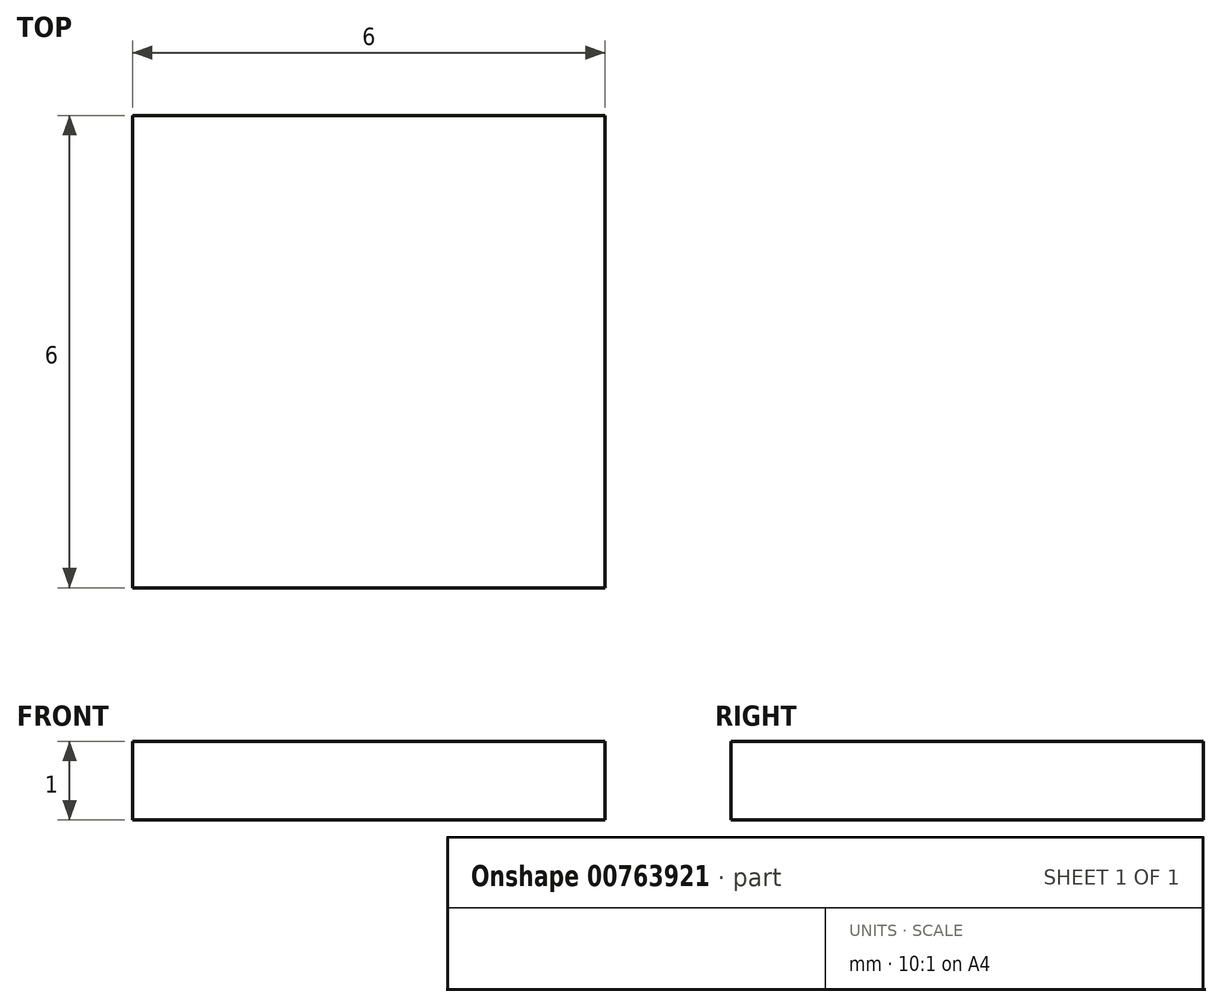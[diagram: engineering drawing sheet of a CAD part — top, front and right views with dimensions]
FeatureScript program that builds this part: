
annotation { "Feature Type Name" : "Feature", "Feature Type Description" : "" }
export const myFeature = defineFeature(function(context is Context, id is Id, definition is map)
    precondition{}
    {
        {
            var Q0;
            Q0=qCreatedBy(makeId("Top.planeOp"),FACE);
            var sketch = newSketch(context, id + "F0", { "sketchPlane" : qUnion([Q0])});
            skLineSegment(sketch, "E0.bottom", {"start": v(3, -3) * mm, "end": v(-3, -3) * mm});
            skLineSegment(sketch, "E0.top", {"start": v(3, 3) * mm, "end": v(-3, 3) * mm});
            skLineSegment(sketch, "E0.left", {"start": v(3, -3) * mm, "end": v(3, 3) * mm});
            skLineSegment(sketch, "E0.right", {"start": v(-3, -3) * mm, "end": v(-3, 3) * mm});
            skPoint(sketch, "E0.middle", {"position": v(0, 0) * mm});
            skSolve(sketch);
        }
        {
            var Q0;
            Q0 = qSketchRegion(id + "F0", true);
            extrude(context, id + "F1", {"entities" : qUnion([Q0]), "depth" : 1 * mm, "offsetDistance" : 25.4 * mm});
        }
    });
